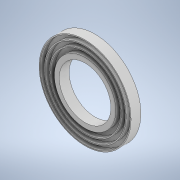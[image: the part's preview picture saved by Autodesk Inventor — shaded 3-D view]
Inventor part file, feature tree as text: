
AUTODESK INVENTOR PART (.ipt)
format: ipt  version: 2021 (Build 250183000, 183)  size: 165,888 bytes
history: native  units: mm
features: sketch x4, plane x4, extrude x3
ambient origin geometry x8: Origin, YZ Plane, XZ Plane, XY Plane, X Axis, Y Axis, Z Axis, Center Point
bodies: Solid1 (feature_tree)
feature tree (11):
  sketch  "Sketch1"  dims[d0=143.0mm d1=147.0mm]
  extrude  "Extrusion1"  Depth=147.0mm
  extrude  "Extrusion2"  Depth=167.0mm
  extrude  "Extrusion3"  Depth=187.0mm
  plane  "Work Plane4"
  sketch  "Sketch3"  dims[d2=163.0mm d3=167.0mm]
  sketch  "Sketch4"  dims[d4=183.0mm d5=187.0mm]
  sketch  "Sketch5"  dims[d6=105.0mm d7=125.0mm d8=10.0mm d9=0.0mm d10=10.0mm d11=0.0mm d12=10.0mm d13=0.0mm d14=10.0mm d15=-5.0mm d16=-5.0mm d17=-5.0mm d18=122.0mm d19=122.0mm d20=122.0mm d22=0.5mm d23=0.872665mm d24=0.5mm d25=0.872665mm d28=0.5mm d29=0.872665mm d30=0.5mm d31=0.872665mm]
  plane  "Work Plane1"
  plane  "Work Plane2"
  plane  "Work Plane3"
